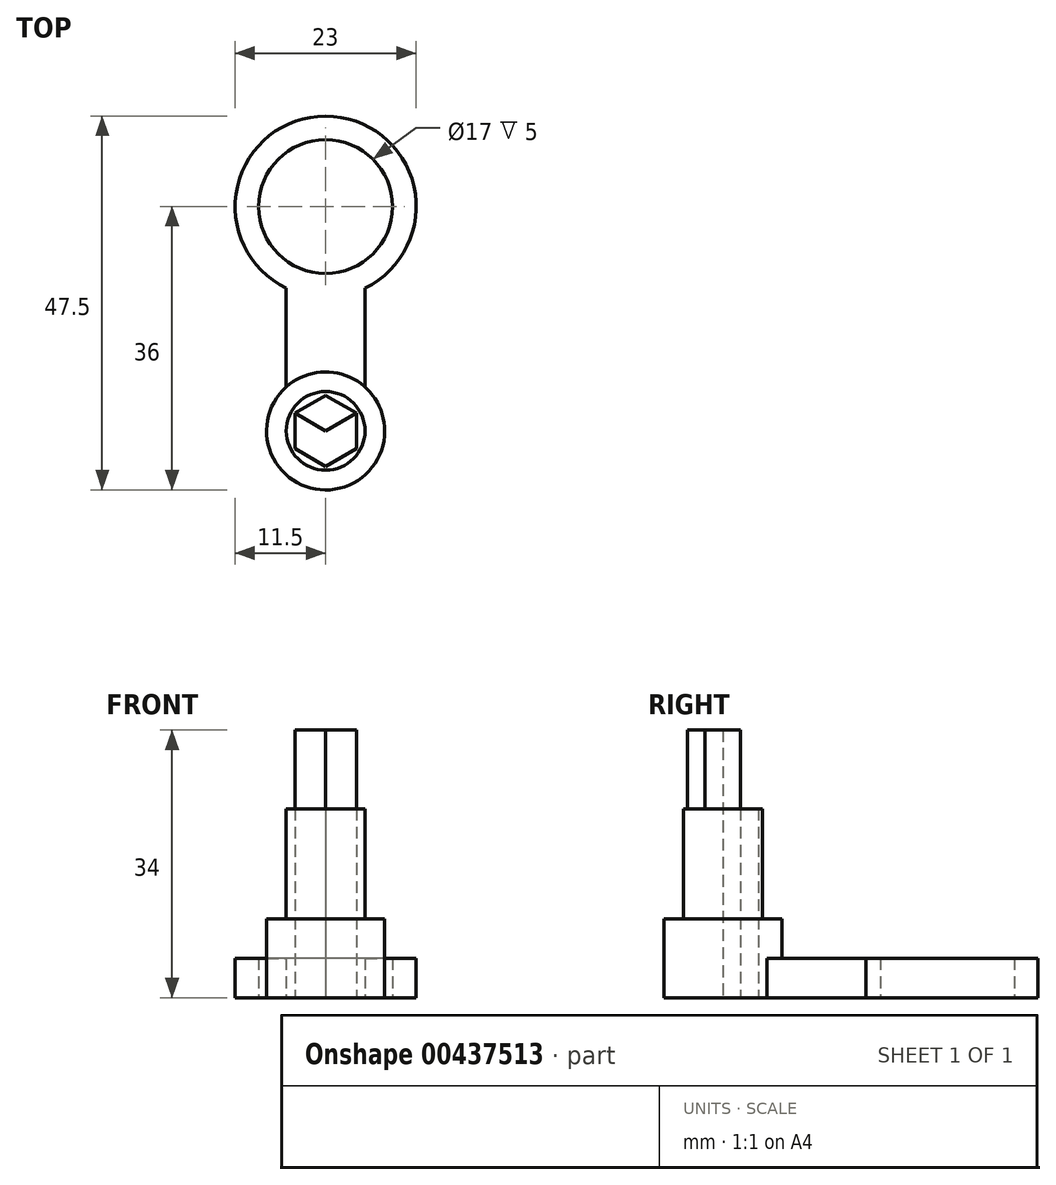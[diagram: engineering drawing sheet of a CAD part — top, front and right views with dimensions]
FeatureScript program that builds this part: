
annotation { "Feature Type Name" : "Feature", "Feature Type Description" : "" }
export const myFeature = defineFeature(function(context is Context, id is Id, definition is map)
    precondition{}
    {
        {
            var Q0;
            Q0=qCreatedBy(makeId("Top.planeOp"),FACE);
            var sketch = newSketch(context, id + "F0", { "sketchPlane" : qUnion([Q0])});
            skCircle(sketch, "E0", {"center": v(0, 0) * mm, "radius": 7.5 * mm});
            skCircle(sketch, "E1", {"center": v(0, 0) * mm, "radius": 5 * mm});
            skLineSegment(sketch, "E2", {"start": v(0, 0) * mm, "end": v(-5, 0) * mm});
            skLineSegment(sketch, "E3", {"start": v(-5, 0) * mm, "end": v(-5, 19.86) * mm});
            skLineSegment(sketch, "E4", {"start": v(-5, 19.86) * mm, "end": v(5, 19.86) * mm});
            skLineSegment(sketch, "E5", {"start": v(5, 19.86) * mm, "end": v(5, 0) * mm});
            skLineSegment(sketch, "E6", {"start": v(5, 0) * mm, "end": v(0, 0) * mm});
            skLineSegment(sketch, "E7", {"start": v(0, 0) * mm, "end": v(0, 40) * mm});
            skCircle(sketch, "E8", {"center": v(0, 28.5) * mm, "radius": 11.5 * mm});
            skCircle(sketch, "E9", {"center": v(0, 28.5) * mm, "radius": 8.5 * mm});
            skLineSegment(sketch, "E10", {"start": v(0, 0) * mm, "end": v(0, 4.5) * mm});
            skLineSegment(sketch, "E11", {"start": v(0, 4.5) * mm, "end": v(3.9, 2.25) * mm});
            skLineSegment(sketch, "E12", {"start": v(3.9, 2.25) * mm, "end": v(3.9, -2.25) * mm});
            skLineSegment(sketch, "E13", {"start": v(3.9, -2.25) * mm, "end": v(0, -4.5) * mm});
            skLineSegment(sketch, "E14", {"start": v(0, -4.5) * mm, "end": v(-3.9, -2.25) * mm});
            skLineSegment(sketch, "E15", {"start": v(-3.9, -2.25) * mm, "end": v(-3.9, 2.25) * mm});
            skLineSegment(sketch, "E16", {"start": v(-3.9, 2.25) * mm, "end": v(0, 4.5) * mm});
            skLineSegment(sketch, "E17", {"start": v(0, 0) * mm, "end": v(-3.9, 2.25) * mm});
            skLineSegment(sketch, "E18", {"start": v(0, 0) * mm, "end": v(-3.9, -2.25) * mm});
            skLineSegment(sketch, "E19", {"start": v(0, 0) * mm, "end": v(0, -4.5) * mm});
            skLineSegment(sketch, "E20", {"start": v(0, 0) * mm, "end": v(3.9, -2.25) * mm});
            skLineSegment(sketch, "E21", {"start": v(0, 0) * mm, "end": v(3.9, 2.25) * mm});
            skSolve(sketch);
        }
        {
            var Q0;
            {var subQ5=sQuery(id+"F0.wireOp",EDGE,"E4");var subQ8=sQuery(id+"F0.wireOp",EDGE,"E3");var subQ9=makeQuery(id+"F0.imprint","INTERSECT",VERTEX,{"derivedFrom":[subQ8,subQ5]});Q0=makeQuery(id+"F0.imprint","IMPRINT",FACE,{"disambiguationData":[TD([[makeQuery(id+"F0.imprint","IMPRINT",EDGE,{"disambiguationData":[TD([[subQ9,1.0]])],"derivedFrom":subQ8}),1.0]])]});}
            var Q1;
            {var subQ5=sQuery(id+"F0.wireOp",EDGE,"E5");var subQ6=sQuery(id+"F0.wireOp",EDGE,"E4");var subQ7=makeQuery(id+"F0.imprint","INTERSECT",VERTEX,{"derivedFrom":[subQ6,subQ5]});Q1=makeQuery(id+"F0.imprint","IMPRINT",FACE,{"disambiguationData":[TD([[makeQuery(id+"F0.imprint","IMPRINT",EDGE,{"disambiguationData":[TD([[subQ7,1.0]])],"derivedFrom":subQ6}),1.0]])]});}
            var Q2;
            {var subQ0=sQuery(id+"F0.wireOp",EDGE,"E5");var subQ1=sQuery(id+"F0.wireOp",EDGE,"E4");var subQ2=makeQuery(id+"F0.imprint","INTERSECT",VERTEX,{"derivedFrom":[subQ1,subQ0]});Q2=makeQuery(id+"F0.imprint","IMPRINT",FACE,{"disambiguationData":[TD([[makeQuery(id+"F0.imprint","IMPRINT",EDGE,{"disambiguationData":[TD([[subQ2,1.0]])],"derivedFrom":subQ1}),-1.0]])]});}
            var Q3;
            {var subQ0=sQuery(id+"F0.wireOp",EDGE,"E4");var subQ1=sQuery(id+"F0.wireOp",EDGE,"E3");var subQ2=makeQuery(id+"F0.imprint","INTERSECT",VERTEX,{"derivedFrom":[subQ1,subQ0]});Q3=makeQuery(id+"F0.imprint","IMPRINT",FACE,{"disambiguationData":[TD([[makeQuery(id+"F0.imprint","IMPRINT",EDGE,{"disambiguationData":[TD([[subQ2,1.0]])],"derivedFrom":subQ1}),-1.0]])]});}
            var Q4;
            {var subQ0=sQuery(id+"F0.wireOp",EDGE,"E3");var subQ1=sQuery(id+"F0.wireOp",EDGE,"E0");var subQ2=makeQuery(id+"F0.imprint","INTERSECT",VERTEX,{"derivedFrom":[subQ1,subQ0]});Q4=makeQuery(id+"F0.imprint","IMPRINT",FACE,{"disambiguationData":[TD([[makeQuery(id+"F0.imprint","IMPRINT",EDGE,{"disambiguationData":[TD([[subQ2,1.0]])],"derivedFrom":subQ1}),-1.0]])]});}
            var Q5;
            {var subQ0=sQuery(id+"F0.wireOp",EDGE,"E5");var subQ1=sQuery(id+"F0.wireOp",EDGE,"E0");var subQ2=makeQuery(id+"F0.imprint","INTERSECT",VERTEX,{"derivedFrom":[subQ1,subQ0]});Q5=makeQuery(id+"F0.imprint","IMPRINT",FACE,{"disambiguationData":[TD([[makeQuery(id+"F0.imprint","IMPRINT",EDGE,{"disambiguationData":[TD([[subQ2,-1.0]])],"derivedFrom":subQ1}),-1.0]])]});}
            extrude(context, id + "F1", {"entities" : qUnion([Q0, Q1, Q2, Q3, Q4, Q5]), "depth" : 5 * mm});
        }
        {
            var Q0;
            {var subQ0=sQuery(id+"F0.wireOp",EDGE,"E5");var subQ1=sQuery(id+"F0.wireOp",EDGE,"E0");var subQ2=makeQuery(id+"F0.imprint","INTERSECT",VERTEX,{"derivedFrom":[subQ1,subQ0]});Q0=makeQuery(id+"F0.imprint","IMPRINT",FACE,{"disambiguationData":[TD([[makeQuery(id+"F0.imprint","IMPRINT",EDGE,{"disambiguationData":[TD([[subQ2,-1.0]])],"derivedFrom":subQ1}),1.0]])]});}
            var Q1;
            {var subQ0=sQuery(id+"F0.wireOp",EDGE,"E5");var subQ1=sQuery(id+"F0.wireOp",EDGE,"E0");var subQ2=makeQuery(id+"F0.imprint","INTERSECT",VERTEX,{"derivedFrom":[subQ1,subQ0]});Q1=makeQuery(id+"F0.imprint","IMPRINT",FACE,{"disambiguationData":[TD([[makeQuery(id+"F0.imprint","IMPRINT",EDGE,{"disambiguationData":[TD([[subQ2,1.0]])],"derivedFrom":subQ1}),1.0]])]});}
            var Q2;
            {var subQ0=sQuery(id+"F0.wireOp",EDGE,"E3");var subQ1=sQuery(id+"F0.wireOp",EDGE,"E0");var subQ2=makeQuery(id+"F0.imprint","INTERSECT",VERTEX,{"derivedFrom":[subQ1,subQ0]});Q2=makeQuery(id+"F0.imprint","IMPRINT",FACE,{"disambiguationData":[TD([[makeQuery(id+"F0.imprint","IMPRINT",EDGE,{"disambiguationData":[TD([[subQ2,1.0]])],"derivedFrom":subQ1}),1.0]])]});}
            extrude(context, id + "F2", {"entities" : qUnion([Q0, Q1, Q2]), "operationType" : NewBodyOperationType.ADD, "depth" : 10 * mm});
        }
        {
            var Q0;
            {var subQ0=sQuery(id+"F0.wireOp",EDGE,"E11");Q0=makeQuery(id+"F0.imprint","IMPRINT",FACE,{"disambiguationData":[TD([[makeQuery(id+"F0.imprint","IMPRINT",EDGE,{"derivedFrom":subQ0}),1.0]])]});}
            var Q1;
            {var subQ0=sQuery(id+"F0.wireOp",EDGE,"E13");Q1=makeQuery(id+"F0.imprint","IMPRINT",FACE,{"disambiguationData":[TD([[makeQuery(id+"F0.imprint","IMPRINT",EDGE,{"derivedFrom":subQ0}),1.0]])]});}
            var Q2;
            {var subQ0=sQuery(id+"F0.wireOp",EDGE,"E16");Q2=makeQuery(id+"F0.imprint","IMPRINT",FACE,{"disambiguationData":[TD([[makeQuery(id+"F0.imprint","IMPRINT",EDGE,{"derivedFrom":subQ0}),1.0]])]});}
            extrude(context, id + "F3", {"entities" : qUnion([Q0, Q1, Q2]), "operationType" : NewBodyOperationType.ADD, "depth" : 24 * mm});
        }
        {
            var Q0;
            Q0=makeQuery(id+"F0.imprint","IMPRINT",FACE,{"disambiguationData":[TD([[makeQuery(id+"F0.imprint","IMPRINT",EDGE,{"derivedFrom":sQuery(id+"F0.wireOp",EDGE,"E10")}),-1.0]])]});
            var Q1;
            {var subQ0=sQuery(id+"F0.wireOp",EDGE,"E21");Q1=makeQuery(id+"F0.imprint","IMPRINT",FACE,{"disambiguationData":[TD([[makeQuery(id+"F0.imprint","IMPRINT",EDGE,{"derivedFrom":subQ0}),-1.0]])]});}
            var Q2;
            {var subQ0=sQuery(id+"F0.wireOp",EDGE,"E20");Q2=makeQuery(id+"F0.imprint","IMPRINT",FACE,{"disambiguationData":[TD([[makeQuery(id+"F0.imprint","IMPRINT",EDGE,{"derivedFrom":subQ0}),1.0]])]});}
            var Q3;
            Q3=makeQuery(id+"F0.imprint","IMPRINT",FACE,{"disambiguationData":[TD([[makeQuery(id+"F0.imprint","IMPRINT",EDGE,{"derivedFrom":sQuery(id+"F0.wireOp",EDGE,"E13")}),-1.0]])]});
            var Q4;
            Q4=makeQuery(id+"F0.imprint","IMPRINT",FACE,{"disambiguationData":[TD([[makeQuery(id+"F0.imprint","IMPRINT",EDGE,{"derivedFrom":sQuery(id+"F0.wireOp",EDGE,"E14")}),-1.0]])]});
            var Q5;
            {var subQ0=sQuery(id+"F0.wireOp",EDGE,"E18");Q5=makeQuery(id+"F0.imprint","IMPRINT",FACE,{"disambiguationData":[TD([[makeQuery(id+"F0.imprint","IMPRINT",EDGE,{"derivedFrom":subQ0}),-1.0]])]});}
            var Q6;
            {var subQ0=sQuery(id+"F0.wireOp",EDGE,"E17");Q6=makeQuery(id+"F0.imprint","IMPRINT",FACE,{"disambiguationData":[TD([[makeQuery(id+"F0.imprint","IMPRINT",EDGE,{"derivedFrom":subQ0}),1.0]])]});}
            var Q7;
            Q7=makeQuery(id+"F0.imprint","IMPRINT",FACE,{"disambiguationData":[TD([[makeQuery(id+"F0.imprint","IMPRINT",EDGE,{"derivedFrom":sQuery(id+"F0.wireOp",EDGE,"E10")}),1.0]])]});
            extrude(context, id + "F4", {"entities" : qUnion([Q0, Q1, Q2, Q3, Q4, Q5, Q6, Q7]), "operationType" : NewBodyOperationType.ADD, "depth" : 34 * mm});
        }
    });
